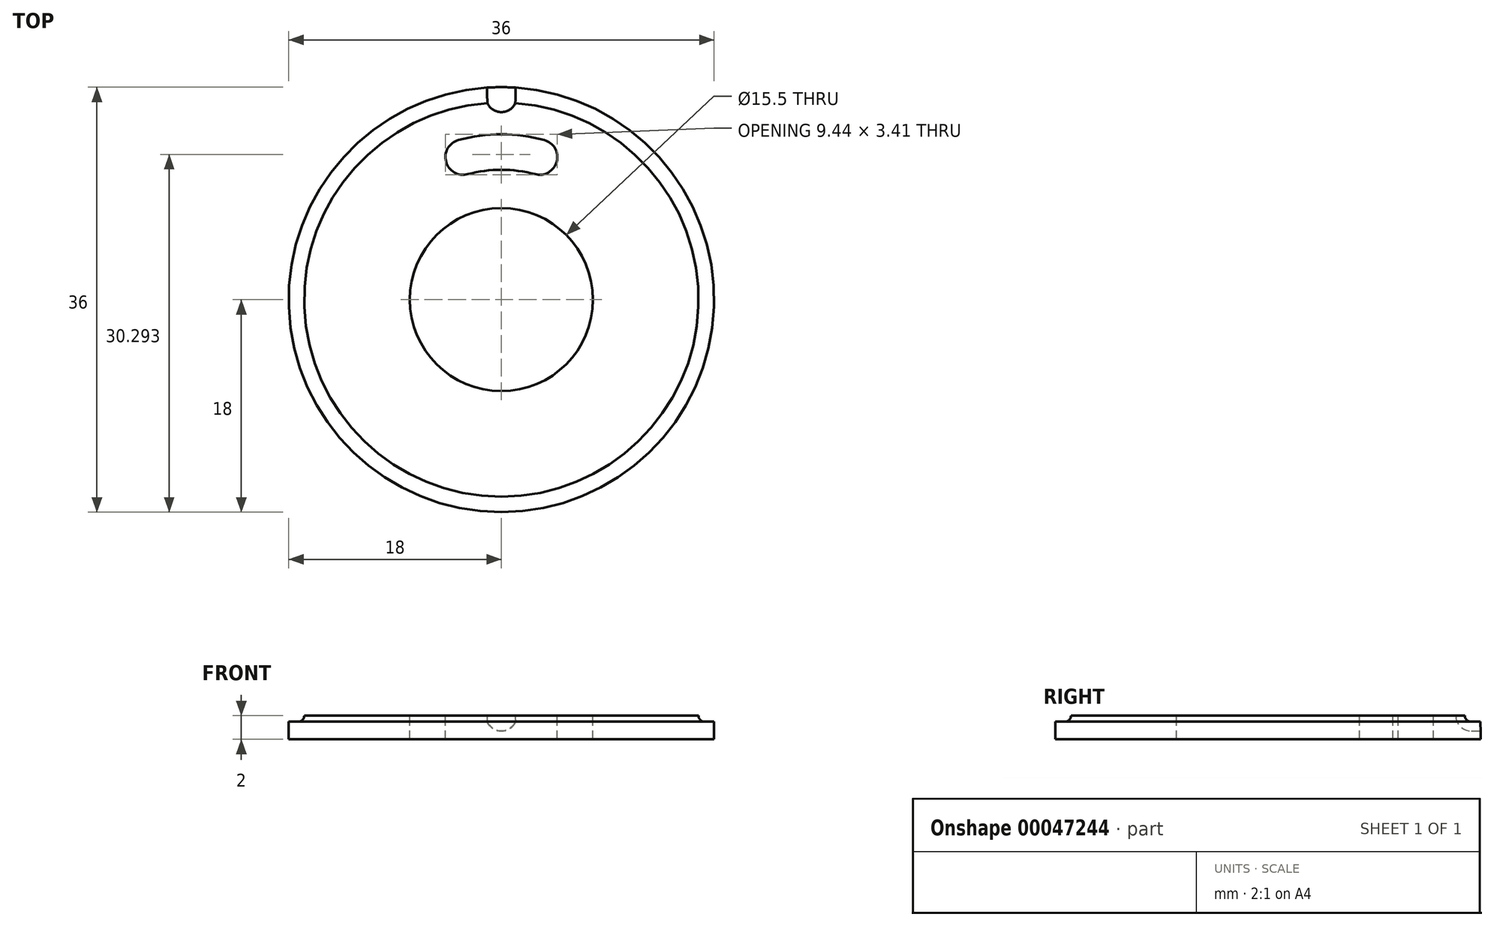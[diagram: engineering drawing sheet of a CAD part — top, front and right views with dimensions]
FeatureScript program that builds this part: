
annotation { "Feature Type Name" : "Feature", "Feature Type Description" : "" }
export const myFeature = defineFeature(function(context is Context, id is Id, definition is map)
    precondition{}
    {
        {
            var Q0;
            Q0=qCreatedBy(makeId("Top.planeOp"),FACE);
            var sketch = newSketch(context, id + "F0", { "sketchPlane" : qUnion([Q0])});
            skCircle(sketch, "E0", {"center": v(0, 0) * mm, "radius": 17.19 * mm});
            skLineSegment(sketch, "E1", {"start": v(0, 0) * mm, "end": v(0, 17.19) * mm});
            skCircle(sketch, "E2", {"center": v(0, 17.19) * mm, "radius": 1.3 * mm});
            skCircle(sketch, "E3", {"center": v(0, 0) * mm, "radius": 18 * mm});
            skSolve(sketch);
        }
        {
            var Q0;
            Q0=qCreatedBy(makeId("Top.planeOp"),FACE);
            var sketch = newSketch(context, id + "F1", { "sketchPlane" : qUnion([Q0])});
            skSolve(sketch);
        }
        {
            var Q0;
            Q0=qSketchRegion(id+"F1",true);
            var Q1;
            {var subQ0=sQuery(id+"F0.wireOp",EDGE,"E2");var subQ1=sQuery(id+"F0.wireOp",EDGE,"E0");var subQ2=makeQuery(id+"F0.imprint","INTERSECT",VERTEX,{"disambiguationData":[OD(0.0)],"derivedFrom":[subQ1,subQ0]});Q1=makeQuery(id+"F0.imprint","IMPRINT",FACE,{"disambiguationData":[TD([[makeQuery(id+"F0.imprint","IMPRINT",EDGE,{"disambiguationData":[TD([[subQ2,1.0]])],"derivedFrom":subQ1}),1.0]])]});}
            var Q2;
            {var subQ0=sQuery(id+"F0.wireOp",EDGE,"E1");var subQ1=sQuery(id+"F0.wireOp",EDGE,"E0");var subQ2=makeQuery(id+"F0.imprint","INTERSECT",VERTEX,{"derivedFrom":[subQ1,subQ0]});Q2=makeQuery(id+"F0.imprint","IMPRINT",FACE,{"disambiguationData":[TD([[makeQuery(id+"F0.imprint","IMPRINT",EDGE,{"disambiguationData":[TD([[subQ2,-1.0]])],"derivedFrom":subQ1}),1.0]])]});}
            var Q3;
            {var subQ0=sQuery(id+"F0.wireOp",EDGE,"E1");var subQ1=sQuery(id+"F0.wireOp",EDGE,"E0");var subQ2=makeQuery(id+"F0.imprint","INTERSECT",VERTEX,{"derivedFrom":[subQ1,subQ0]});Q3=makeQuery(id+"F0.imprint","IMPRINT",FACE,{"disambiguationData":[TD([[makeQuery(id+"F0.imprint","IMPRINT",EDGE,{"disambiguationData":[TD([[subQ2,1.0]])],"derivedFrom":subQ1}),1.0]])]});}
            var Q4;
            {var subQ0=sQuery(id+"F0.wireOp",EDGE,"E2");var subQ1=sQuery(id+"F0.wireOp",EDGE,"E0");var subQ2=makeQuery(id+"F0.imprint","INTERSECT",VERTEX,{"disambiguationData":[OD(0.0)],"derivedFrom":[subQ1,subQ0]});Q4=makeQuery(id+"F0.imprint","IMPRINT",FACE,{"disambiguationData":[TD([[makeQuery(id+"F0.imprint","IMPRINT",EDGE,{"disambiguationData":[TD([[subQ2,1.0]])],"derivedFrom":subQ1}),-1.0]])]});}
            var Q5;
            {var subQ3=sQuery(id+"F0.wireOp",EDGE,"E0");var subQ5=makeQuery(id+"F0.imprint","INTERSECT",VERTEX,{"derivedFrom":[subQ3,sQuery(id+"F0.wireOp",EDGE,"E1")]});Q5=makeQuery(id+"F0.imprint","IMPRINT",FACE,{"disambiguationData":[TD([[makeQuery(id+"F0.imprint","IMPRINT",EDGE,{"disambiguationData":[TD([[subQ5,1.0]])],"derivedFrom":subQ3}),-1.0]])]});}
            extrude(context, id + "F2", {"entities" : qUnion([Q0, Q1, Q2, Q3, Q4, Q5]), "depth" : 4 * mm});
        }
        {
            var Q0;
            Q0=qCreatedBy(makeId("Top.planeOp"),FACE);
            var Q1;
            Q1=makeQuery(id+"F2.opExtrude","CAP_FACE",FACE,{"disambiguationData":[OSD([sQuery(id+"F0.wireOp",EDGE,"E3")])],"isStart":false});
            cPlane(context, id + "F3", {"entities" : qUnion([Q0, Q1]), "cplaneType" : CPlaneType.MID_PLANE, "offset" : 25 * mm, "width" : 150 * mm, "height" : 150 * mm});
        }
        {
            var Q0;
            Q0=qCreatedBy(id+"F3.planeOp",FACE);
            var sketch = newSketch(context, id + "F4", { "sketchPlane" : qUnion([Q0])});
            skArc(sketch, "E4.0", {"start": v(0, 15.89) * mm, "mid": v(1.3, 17.19) * mm, "end": v(0, 18.49) * mm});
            skLineSegment(sketch, "E5", {"start": v(0, 15.89) * mm, "end": v(0, 18.49) * mm});
            skLineSegment(sketch, "E6", {"start": v(0, 17.19) * mm, "end": v(1.3, 17.19) * mm});
            skLineSegment(sketch, "E7", {"start": v(1.3, 17.19) * mm, "end": v(1.3, 18.49) * mm});
            skLineSegment(sketch, "E8", {"start": v(1.3, 18.49) * mm, "end": v(0, 18.49) * mm});
            skSolve(sketch);
        }
        {
            var Q0;
            Q0=makeQuery(id+"F4.imprint","IMPRINT",FACE,{"disambiguationData":[TD([[makeQuery(id+"F4.imprint","IMPRINT",EDGE,{"derivedFrom":sQuery(id+"F4.wireOp",EDGE,"E4.0")}),1.0]])]});
            var Q1;
            {var subQ2=sQuery(id+"F4.wireOp",EDGE,"E7");Q1=makeQuery(id+"F4.imprint","IMPRINT",FACE,{"disambiguationData":[TD([[makeQuery(id+"F4.imprint","IMPRINT",EDGE,{"derivedFrom":subQ2}),1.0]])]});}
            var Q2;
            Q2=sQuery(id+"F4.wireOp",EDGE,"E5");
            revolve(context, id + "F5", {"operationType" : NewBodyOperationType.REMOVE, "entities" : qUnion([Q0, Q1]), "axis" : qUnion([Q2]), "revolveType" : RevolveType.FULL, "oppositeDirection" : true});
        }
        {
            var Q0;
            Q0=qCreatedBy(makeId("Front.planeOp"),FACE);
            var sketch = newSketch(context, id + "F6", { "sketchPlane" : qUnion([Q0])});
            skLineSegment(sketch, "E9.0", {"start": v(-17.19, 4) * mm, "end": v(17.19, 4) * mm, "construction": true});
            skLineSegment(sketch, "E9.1", {"start": v(-17.19, 0) * mm, "end": v(17.19, 0) * mm, "construction": true});
            skLineSegment(sketch, "E10", {"start": v(0, 0) * mm, "end": v(0, 4) * mm, "construction": true});
            skLineSegment(sketch, "E11", {"start": v(0, 2) * mm, "end": v(17.19, 2) * mm, "construction": true});
            skArc(sketch, "E12", {"start": v(17.19, 2.5) * mm, "mid": v(16.69, 2) * mm, "end": v(17.19, 1.5) * mm});
            skLineSegment(sketch, "E13", {"start": v(16.69, 2) * mm, "end": v(16.56, 2) * mm, "construction": true});
            skLineSegment(sketch, "E14", {"start": v(17.19, 2.5) * mm, "end": v(18.21, 2.5) * mm});
            skLineSegment(sketch, "E15", {"start": v(18.21, 2.5) * mm, "end": v(18.21, 1.5) * mm});
            skLineSegment(sketch, "E16", {"start": v(17.19, 1.5) * mm, "end": v(18.21, 1.5) * mm});
            skSolve(sketch);
        }
        {
            var Q0;
            {var subQ1=sQuery(id+"F6.wireOp",EDGE,"E12");var subQ6=sQuery(id+"F6.wireOp",EDGE,"Q5owe86Z-UdA3-Mzv4-9Ln9-rBpZI1dkmUp1");var subQ8=makeQuery(id+"F6.imprint","INTERSECT",VERTEX,{"disambiguationData":[OD(0.0)],"derivedFrom":[subQ1,subQ6]});Q0=makeQuery(id+"F6.imprint","IMPRINT",FACE,{"disambiguationData":[TD([[makeQuery(id+"F6.imprint","IMPRINT",EDGE,{"disambiguationData":[TD([[subQ8,1.0]])],"derivedFrom":subQ1}),1.0]])]});}
            var Q1;
            {var subQ0=sQuery(id+"F6.wireOp",EDGE,"Q5owe86Z-UdA3-Mzv4-9Ln9-rBpZI1dkmUp1");var subQ1=sQuery(id+"F6.wireOp",EDGE,"E12");var subQ2=makeQuery(id+"F6.imprint","INTERSECT",VERTEX,{"disambiguationData":[OD(0.0)],"derivedFrom":[subQ1,subQ0]});Q1=makeQuery(id+"F6.imprint","IMPRINT",FACE,{"disambiguationData":[TD([[makeQuery(id+"F6.imprint","IMPRINT",EDGE,{"disambiguationData":[TD([[subQ2,1.0]])],"derivedFrom":subQ1}),-1.0]])]});}
            var Q2;
            {var subQ0=sQuery(id+"F6.wireOp",EDGE,"TDUslP9x-rfeX-e3iP-snPt-IsEtmXCtfriO");var subQ1=sQuery(id+"F6.wireOp",EDGE,"E12");var subQ2=makeQuery(id+"F6.imprint","INTERSECT",VERTEX,{"disambiguationData":[OD(1.0)],"derivedFrom":[subQ1,subQ0]});Q2=makeQuery(id+"F6.imprint","IMPRINT",FACE,{"disambiguationData":[TD([[makeQuery(id+"F6.imprint","IMPRINT",EDGE,{"disambiguationData":[TD([[subQ2,-1.0]])],"derivedFrom":subQ1}),-1.0]])]});}
            var Q3;
            Q3=sQuery(id+"F0.wireOp",EDGE,"E0");
            revolve(context, id + "F7", {"operationType" : NewBodyOperationType.REMOVE, "entities" : qUnion([Q0, Q1, Q2]), "axis" : qUnion([Q3]), "revolveType" : RevolveType.FULL, "oppositeDirection" : true});
        }
        {
            var Q0;
            Q0=makeQuery(id+"F2.opExtrude","CAP_FACE",FACE,{"disambiguationData":[OSD([sQuery(id+"F0.wireOp",EDGE,"E3")])],"isStart":false});
            var sketch = newSketch(context, id + "F8", { "sketchPlane" : qUnion([Q0])});
            skCircle(sketch, "E17", {"center": v(0, 0) * mm, "radius": 7.75 * mm});
            skSolve(sketch);
        }
        {
            var Q0;
            Q0=qSketchRegion(id+"F8",true);
            extrude(context, id + "F9", {"entities" : qUnion([Q0]), "operationType" : NewBodyOperationType.REMOVE, "oppositeDirection" : true, "depth" : 25 * mm});
        }
        {
            var Q0;
            Q0=makeQuery(id+"F2.opExtrude","CAP_FACE",FACE,{"disambiguationData":[OSD([sQuery(id+"F0.wireOp",EDGE,"E3")])],"isStart":false});
            var sketch = newSketch(context, id + "F10", { "sketchPlane" : qUnion([Q0])});
            skCircle(sketch, "E18", {"center": v(0, 0) * mm, "radius": 56.26 * mm});
            skSolve(sketch);
        }
        {
            var Q0;
            Q0=qSketchRegion(id+"F10",true);
            extrude(context, id + "F11", {"entities" : qUnion([Q0]), "operationType" : NewBodyOperationType.REMOVE, "oppositeDirection" : true, "depth" : 2 * mm});
        }
        {
            var Q0;
            Q0=makeQuery(id+"F11.boolean.opBoolean","COPY",FACE,{"derivedFrom":makeQuery(id+"F11.opExtrude","CAP_FACE",FACE,{"disambiguationData":[OSD([sQuery(id+"F10.wireOp",EDGE,"E18")])],"isStart":false})});
            var sketch = newSketch(context, id + "F12", { "sketchPlane" : qUnion([Q0])});
            skCircle(sketch, "E19.0", {"center": v(0, 0) * mm, "radius": 7.75 * mm, "construction": true});
            skCircle(sketch, "E19.1", {"center": v(0, 17.19) * mm, "radius": 1.3 * mm, "construction": true});
            skLineSegment(sketch, "E20", {"start": v(0, 7.75) * mm, "end": v(0, 15.89) * mm, "construction": true});
            skCircle(sketch, "E21", {"center": v(0, 0) * mm, "radius": 12.5 * mm, "construction": true});
            skLineSegment(sketch, "E22", {"start": v(0, 0) * mm, "end": v(3.24, 12.07) * mm, "construction": true});
            skLineSegment(sketch, "E23", {"start": v(0, 0) * mm, "end": v(-3.24, 12.07) * mm, "construction": true});
            skArc(sketch, "E24", {"start": v(-3.62, 13.52) * mm, "mid": v(-4.68, 11.69) * mm, "end": v(-2.85, 10.63) * mm});
            skArc(sketch, "E25", {"start": v(2.85, 10.63) * mm, "mid": v(4.68, 11.69) * mm, "end": v(3.62, 13.52) * mm});
            skArc(sketch, "E26", {"start": v(2.85, 10.63) * mm, "mid": v(0, 11) * mm, "end": v(-2.85, 10.63) * mm});
            skArc(sketch, "E27", {"start": v(3.62, 13.52) * mm, "mid": v(0, 14) * mm, "end": v(-3.62, 13.52) * mm});
            skSolve(sketch);
        }
        {
            var Q0;
            Q0 = qSketchRegion(id + "F12", true);
            extrude(context, id + "F13", {"entities" : qUnion([Q0]), "operationType" : NewBodyOperationType.REMOVE, "oppositeDirection" : true, "depth" : 25 * mm});
        }
    });
